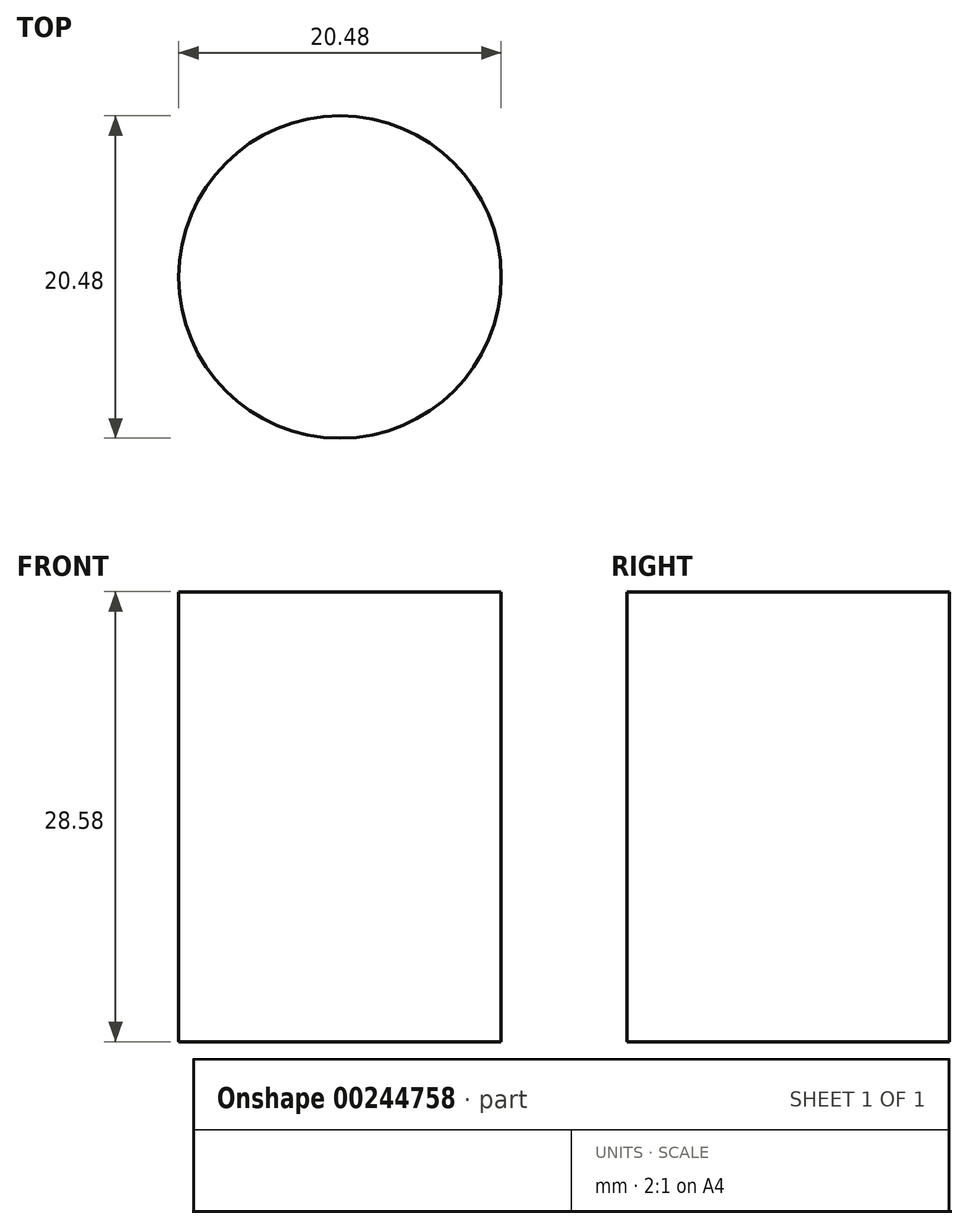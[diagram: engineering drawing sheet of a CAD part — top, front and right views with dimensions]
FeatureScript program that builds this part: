
annotation { "Feature Type Name" : "Feature", "Feature Type Description" : "" }
export const myFeature = defineFeature(function(context is Context, id is Id, definition is map)
    precondition{}
    {
        {
            var Q0;
            Q0=qCreatedBy(makeId("Top.planeOp"),FACE);
            var sketch = newSketch(context, id + "F0", { "sketchPlane" : qUnion([Q0])});
            skCircle(sketch, "E0", {"center": v(0, 0) * mm, "radius": 10.24 * mm});
            skSolve(sketch);
        }
        {
            var Q0;
            Q0 = qSketchRegion(id + "F0", true);
            extrude(context, id + "F1", {"entities" : qUnion([Q0]), "depth" : 28.57 * mm});
        }
    });
